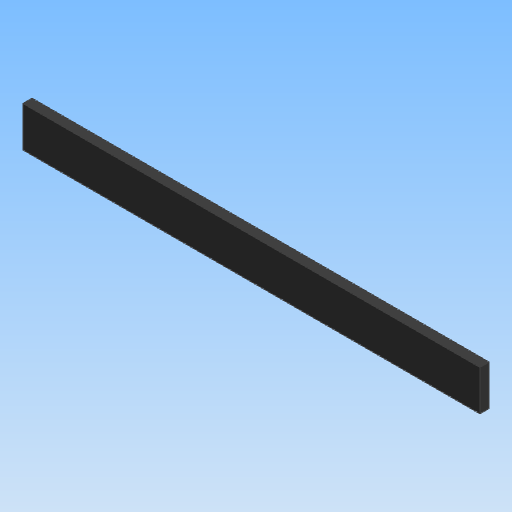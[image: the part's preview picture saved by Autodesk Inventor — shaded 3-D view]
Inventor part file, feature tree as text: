
AUTODESK INVENTOR PART (.ipt)
format: ipt  version: 2020 (Build 240168000, 168)  size: 82,432 bytes
history: native  units: mm
features: other x1, extrude x1
ambient origin geometry x8: Origin, YZ Plane, XZ Plane, XY Plane, X Axis, Y Axis, Z Axis, Center Point
bodies: Body1 (feature_tree)
feature tree (2):
  other  "實體1"
  extrude  "擠出1"  Depth=11.0mm
